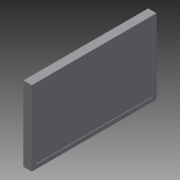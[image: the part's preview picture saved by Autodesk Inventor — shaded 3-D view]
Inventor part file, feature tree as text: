
AUTODESK INVENTOR PART (.ipt)
format: ipt  version: 2015 SP1 (Build 190203100, 203)  size: 81,920 bytes
history: native  units: in
note: dims shown in document units (in); Inventor stores cm internally (conversion verified against a paired STEP export)
features: extrude x2, sketch x2
ambient origin geometry x8: Origin, YZ Plane, XZ Plane, XY Plane, X Axis, Y Axis, Z Axis, Center Point
bodies: Solid1 (feature_tree)
feature tree (4):
  extrude  "Extrusion1"  Depth=18.0in
  extrude  "Extrusion2"  Depth=1.0in
  sketch  "Sketch1"  dims[d0=30.0in d1=18.0in]
  sketch  "Sketch2"  dims[d2=2.0in d3=0.0in d4=1.0in d5=0.1in d6=0.0in]
